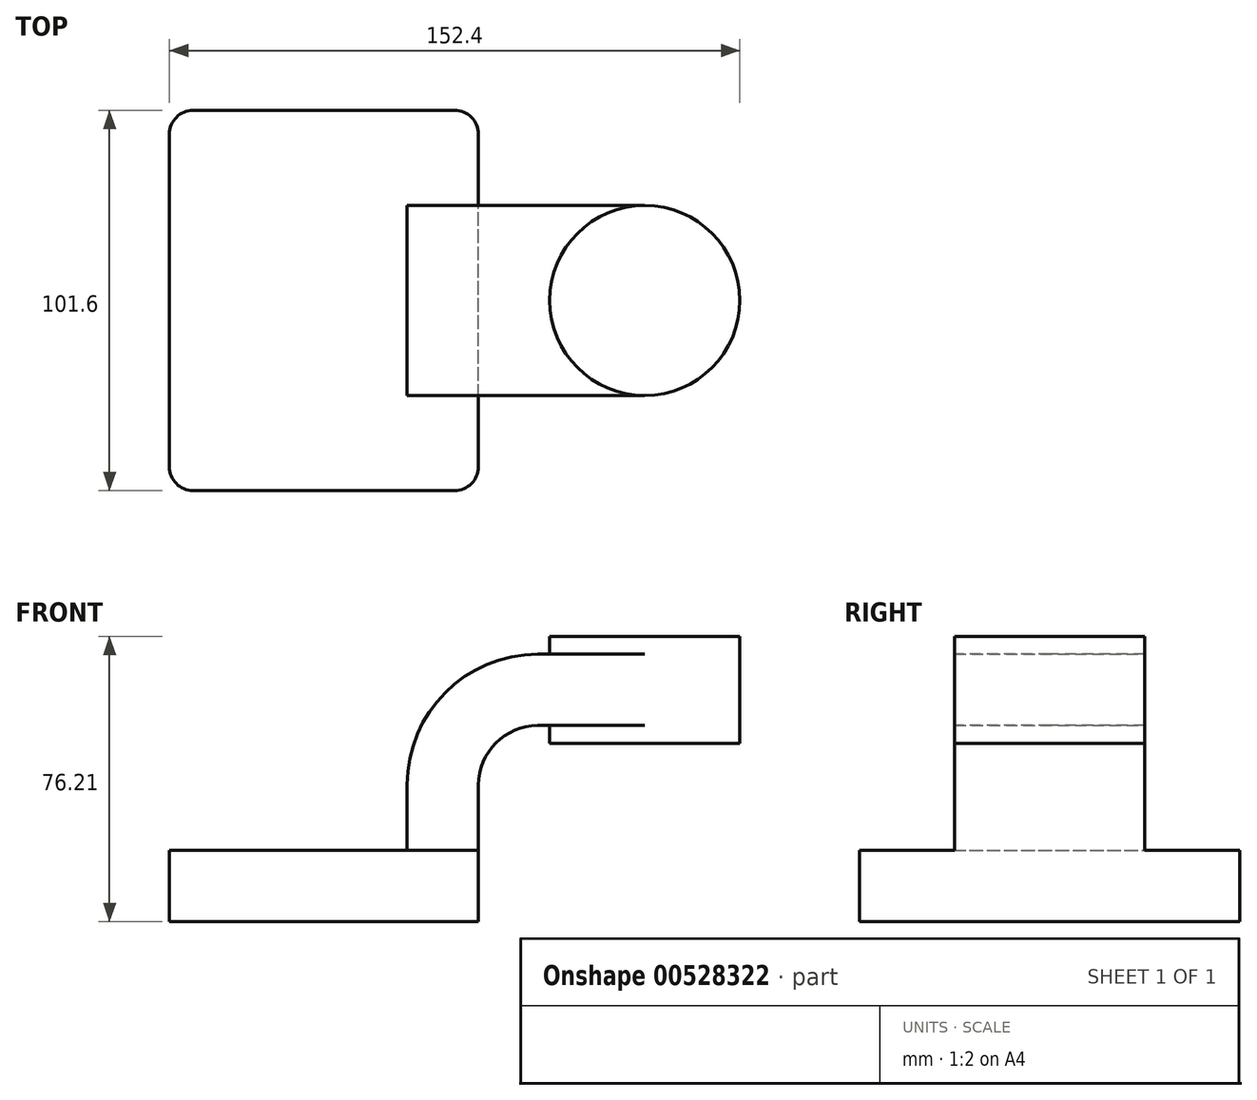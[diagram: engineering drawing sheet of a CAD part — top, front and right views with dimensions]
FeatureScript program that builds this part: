
annotation { "Feature Type Name" : "Feature", "Feature Type Description" : "" }
export const myFeature = defineFeature(function(context is Context, id is Id, definition is map)
    precondition{}
    {
        {
            var Q0;
            Q0=qCreatedBy(makeId("Front.planeOp"),FACE);
            var sketch = newSketch(context, id + "F0", { "sketchPlane" : qUnion([Q0])});
            skLineSegment(sketch, "E0.bottom", {"start": v(41.27, 9.53) * mm, "end": v(-41.28, 9.53) * mm});
            skLineSegment(sketch, "E0.top", {"start": v(41.28, -9.53) * mm, "end": v(-41.27, -9.53) * mm});
            skLineSegment(sketch, "E0.left", {"start": v(41.27, 9.53) * mm, "end": v(41.27, -9.52) * mm});
            skLineSegment(sketch, "E0.right", {"start": v(-41.28, 9.53) * mm, "end": v(-41.28, -9.52) * mm});
            skPoint(sketch, "E0.middle", {"position": v(0, 0) * mm});
            skLineSegment(sketch, "E1.bottom", {"start": v(111.12, 38.1) * mm, "end": v(60.33, 38.1) * mm});
            skLineSegment(sketch, "E1.top", {"start": v(111.13, 66.68) * mm, "end": v(60.33, 66.68) * mm});
            skLineSegment(sketch, "E1.left", {"start": v(111.13, 38.1) * mm, "end": v(111.13, 66.68) * mm});
            skLineSegment(sketch, "E1.right", {"start": v(60.33, 38.1) * mm, "end": v(60.33, 66.68) * mm});
            skPoint(sketch, "E1.middle", {"position": v(85.73, 52.39) * mm});
            skLineSegment(sketch, "E2", {"start": v(41.27, 9.53) * mm, "end": v(41.27, 27) * mm});
            skArc(sketch, "E3", {"start": v(41.27, 27) * mm, "mid": v(45.92, 38.23) * mm, "end": v(57.15, 42.88) * mm});
            skLineSegment(sketch, "E4", {"start": v(57.15, 42.88) * mm, "end": v(85.73, 42.88) * mm});
            skLineSegment(sketch, "E5.0", {"start": v(57.15, 61.93) * mm, "end": v(85.73, 61.93) * mm});
            skArc(sketch, "E5.1", {"start": v(22.23, 27) * mm, "mid": v(32.45, 51.7) * mm, "end": v(57.15, 61.93) * mm});
            skLineSegment(sketch, "E5.2", {"start": v(22.22, 9.53) * mm, "end": v(22.22, 27) * mm});
            skLineSegment(sketch, "E6", {"start": v(85.73, 38.1) * mm, "end": v(85.73, 66.68) * mm});
            skFitSpline(sketch, "E7", {"points": [v(-41.27, 9.53) * mm, v(57.15, 61.93) * mm], "startDerivative": vector(0, 77.05) * mm, "endDerivative": vector(119.57, 0) * mm});
            skSolve(sketch);
        }
        {
            var Q0;
            Q0=makeQuery(id+"F0.imprint","IMPRINT",FACE,{"disambiguationData":[TD([[makeQuery(id+"F0.imprint","IMPRINT",EDGE,{"derivedFrom":sQuery(id+"F0.wireOp",EDGE,"E0.top")}),-1.0]])]});
            extrude(context, id + "F1", {"entities" : qUnion([Q0]), "endBound" : BoundingType.SYMMETRIC, "depth" : 101.6 * mm, "offsetDistance" : 25.4 * mm});
        }
        {
            var Q0;
            {var subQ1=sQuery(id+"F0.wireOp",EDGE,"E2");Q0=makeQuery(id+"F0.imprint","IMPRINT",FACE,{"disambiguationData":[TD([[makeQuery(id+"F0.imprint","IMPRINT",EDGE,{"derivedFrom":subQ1}),1.0]])]});}
            var Q1;
            {var subQ0=sQuery(id+"F0.wireOp",EDGE,"E4");var subQ1=sQuery(id+"F0.wireOp",EDGE,"E1.right");var subQ2=makeQuery(id+"F0.imprint","INTERSECT",VERTEX,{"derivedFrom":[subQ1,subQ0]});Q1=makeQuery(id+"F0.imprint","IMPRINT",FACE,{"disambiguationData":[TD([[makeQuery(id+"F0.imprint","IMPRINT",EDGE,{"disambiguationData":[TD([[subQ2,-1.0]])],"derivedFrom":subQ1}),-1.0]])]});}
            extrude(context, id + "F2", {"entities" : qUnion([Q0, Q1]), "operationType" : NewBodyOperationType.ADD, "endBound" : BoundingType.SYMMETRIC, "depth" : 50.8 * mm, "offsetDistance" : 25.4 * mm});
        }
        {
            var Q0;
            Q0=makeQuery(id+"F0.imprint","IMPRINT",FACE,{"disambiguationData":[TD([[makeQuery(id+"F0.imprint","IMPRINT",EDGE,{"derivedFrom":sQuery(id+"F0.wireOp",EDGE,"E5.1")}),1.0]])]});
            extrude(context, id + "F3", {"entities" : qUnion([Q0]), "operationType" : NewBodyOperationType.ADD, "endBound" : BoundingType.SYMMETRIC, "depth" : 15.88 * mm, "offsetDistance" : 25.4 * mm});
        }
        {
            var Q0;
            {var subQ4=sQuery(id+"F0.wireOp",EDGE,"E1.left");Q0=makeQuery(id+"F0.imprint","IMPRINT",FACE,{"disambiguationData":[TD([[makeQuery(id+"F0.imprint","IMPRINT",EDGE,{"derivedFrom":subQ4}),1.0]])]});}
            var Q1;
            Q1=sQuery(id+"F0.wireOp",EDGE,"E6");
            revolve(context, id + "F4", {"operationType" : NewBodyOperationType.ADD, "entities" : qUnion([Q0]), "axis" : qUnion([Q1]), "revolveType" : RevolveType.FULL});
        }
        {
            var Q0;
            Q0=makeQuery(id+"F1.opExtrude","CAP_EDGE",EDGE,{"disambiguationData":[OSD([sQuery(id+"F0.wireOp",EDGE,"E0.left")])],"isStart":false});
            var Q1;
            Q1=makeQuery(id+"F1.opExtrude","CAP_EDGE",EDGE,{"disambiguationData":[OSD([sQuery(id+"F0.wireOp",EDGE,"E0.right")])],"isStart":false});
            var Q2;
            Q2=makeQuery(id+"F1.opExtrude","CAP_EDGE",EDGE,{"disambiguationData":[OSD([sQuery(id+"F0.wireOp",EDGE,"E0.left")])],"isStart":true});
            var Q3;
            Q3=makeQuery(id+"F1.opExtrude","CAP_EDGE",EDGE,{"disambiguationData":[OSD([sQuery(id+"F0.wireOp",EDGE,"E0.right")])],"isStart":true});
            fillet(context, id + "F5", {"entities" : qUnion([Q0, Q1, Q2, Q3]), "radius" : 6.35 * mm, "tangentPropagation" : true, "allowEdgeOverflow" : false});
        }
    });
